FCSTD DOCUMENT  (FreeCAD 1.0R39109 (Git))
Label: RC1_assembly
License: All rights reserved
LicenseURL: http://en.wikipedia.org/wiki/All_rights_reserved
objects: App::Link×5, App::FeaturePython×3, Assembly::JointGroup×1, Assembly::AssemblyObject×1
EXTERNAL_REF file=RC1_main.FCStd obj=Body
EXTERNAL_REF file=RC1_main.FCStd obj=Feature003
EXTERNAL_REF file=RC1_main.FCStd obj=Feature002
EXTERNAL_REF file=RC1_main.FCStd obj=Feature001
EXTERNAL_REF file=RC1_main.FCStd obj=Feature

FEATURE [App::Link] housing
  LinkedObject = -> <external RC1_main.FCStd>#Body
FEATURE [App::FeaturePython] GroundedJoint  # Assembly grounded joint (typed FeaturePython)
  ObjectToGround = -> housing
FEATURE [App::Link] airMouse_thumb  label="airMouse-thumb"
  LinkPlacement = pos=(-38,-144,7) rot=(0,0,1;1.5708rad)
  LinkedObject = -> <external RC1_main.FCStd>#Feature003
  Placement = pos=(-38,-144,7) rot=(0,0,1;1.5708rad)
FEATURE [App::Link] airMouse_mouse  label="airMouse-mouse"
  LinkPlacement = pos=(67,161,7) rot=(0,0,-1;1.5708rad)
  LinkedObject = -> <external RC1_main.FCStd>#Feature002
  Placement = pos=(67,161,7) rot=(0,0,-1;1.5708rad)
FEATURE [App::Link] airMouse_keyboard  label="airMouse-keyboard"
  LinkPlacement = pos=(-113.25,67,2) rot=(0,0,1;0rad)
  LinkedObject = -> <external RC1_main.FCStd>#Feature001
  Placement = pos=(-113.25,67,2) rot=(0,0,1;0rad)
FEATURE [App::FeaturePython] Joint  label="Fixed"  # Assembly joint (typed FeaturePython)
  Activated = true
  AngleMax = 0
  AngleMin = 0
  Detach1 = false
  Detach2 = false
  Distance = 0
  Distance2 = 0
  EnableAngleMax = false
  EnableAngleMin = false
  EnableLengthMax = false
  EnableLengthMin = false
  JointType = 0 (Fixed)
  LengthMax = 0
  LengthMin = 0
  Offset2 = pos=(0,0,0) rot=(0,0,-1;1.5708rad)
  Placement1 = pos=(-23.25,-10,2) rot=(0,0,1;0rad)
  Placement2 = pos=(90,-77,0) rot=(-1,0,0;3.14159rad)
  Reference1 = -> Assembly [housing.Edge226,housing.Edge226]
  Reference2 = -> Assembly [airMouse_keyboard.Edge9569,airMouse_keyboard.Edge9569]
FEATURE [App::Link] airMouse_mcu  label="airMouse-mcu"
  LinkPlacement = pos=(-128.25,139,2) rot=(0,0,1;0rad)
  LinkedObject = -> <external RC1_main.FCStd>#Feature
  Placement = pos=(-128.25,139,2) rot=(0,0,1;0rad)
FEATURE [App::FeaturePython] Joint001  label="Fixed001"  # Assembly joint (typed FeaturePython)
  Activated = true
  AngleMax = 0
  AngleMin = 0
  Detach1 = false
  Detach2 = false
  Distance = 0
  Distance2 = 0
  EnableAngleMax = false
  EnableAngleMin = false
  EnableLengthMax = false
  EnableLengthMin = false
  JointType = 0 (Fixed)
  LengthMax = 0
  LengthMin = 0
  Offset2 = pos=(0,0,0) rot=(0,0,-1;1.5708rad)
  Placement1 = pos=(141,-119,0) rot=(-0.707107,0.707107,0;3.14159rad)
  Placement2 = pos=(12.75,20,2) rot=(0,0,-1;1.5708rad)
  Reference1 = -> Assembly [airMouse_mcu.Edge11555,airMouse_mcu.Edge11555]
  Reference2 = -> Assembly [housing.Edge246,housing.Edge246]
FEATURE [Assembly::JointGroup] Joints
  Group = -> [GroundedJoint,Joint,Joint001]
FEATURE [Assembly::AssemblyObject] Assembly
  Group = -> [Joints,housing,GroundedJoint,airMouse_thumb,airMouse_mouse,airMouse_keyboard,Joint,airMouse_mcu,Joint001]
  Origin = -> Origin
  Type = Assembly

RESOLVED EXTERNAL PARTS (link-assembly join: the EXTERNAL_REF files above that resolve inside this repo's crawl, each included once):
---- part RC1_main.FCStd = doc fcstd_8bb34e4cbb13 (145684 chars; too large to inline — full recipe in that document) ----
